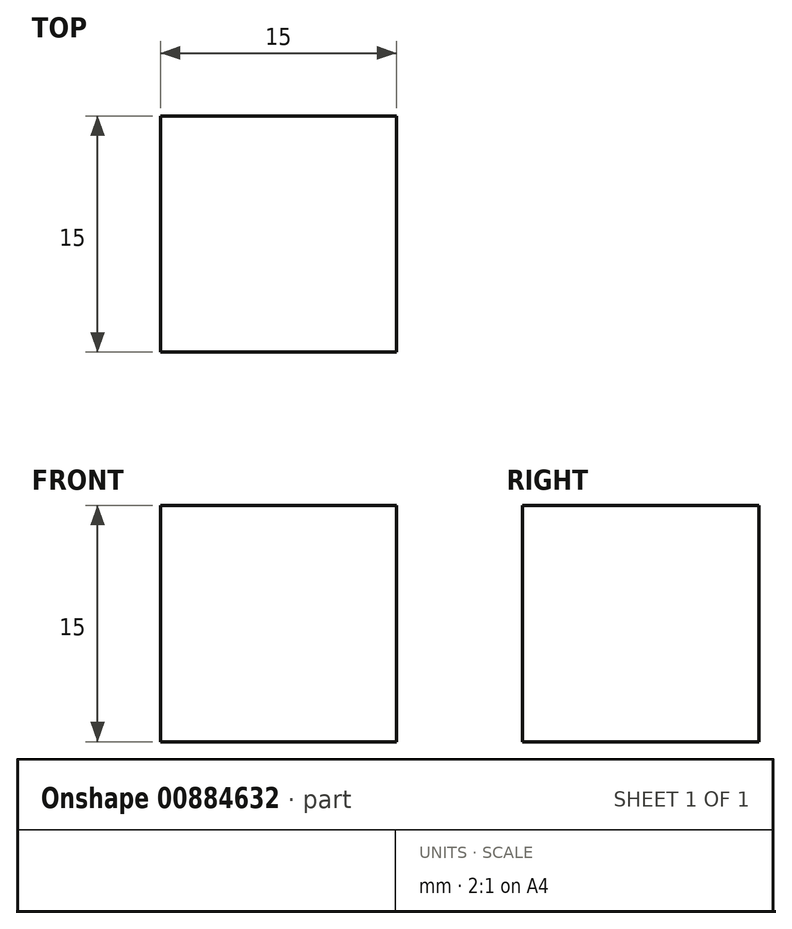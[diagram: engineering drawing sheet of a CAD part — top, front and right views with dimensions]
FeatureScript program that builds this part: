
annotation { "Feature Type Name" : "Feature", "Feature Type Description" : "" }
export const myFeature = defineFeature(function(context is Context, id is Id, definition is map)
    precondition{}
    {
        {
            var Q0;
            Q0=qCreatedBy(makeId("Front.planeOp"),FACE);
            var sketch = newSketch(context, id + "F0", { "sketchPlane" : qUnion([Q0])});
            skLineSegment(sketch, "E0.bottom", {"start": v(0, 0) * mm, "end": v(15, 0) * mm});
            skLineSegment(sketch, "E0.top", {"start": v(0, 15) * mm, "end": v(15, 15) * mm});
            skLineSegment(sketch, "E0.left", {"start": v(0, 0) * mm, "end": v(0, 15) * mm});
            skLineSegment(sketch, "E0.right", {"start": v(15, 0) * mm, "end": v(15, 15) * mm});
            skLineSegment(sketch, "E1.0.1.0", {"start": v(15, 15) * mm, "end": v(15, 30) * mm});
            skLineSegment(sketch, "E1.0.1.1", {"start": v(0, 15) * mm, "end": v(0, 30) * mm});
            skLineSegment(sketch, "E1.0.1.2", {"start": v(0, 30) * mm, "end": v(15, 30) * mm});
            skLineSegment(sketch, "E1.0.2.0", {"start": v(15, 30) * mm, "end": v(15, 45) * mm});
            skLineSegment(sketch, "E1.0.2.1", {"start": v(0, 30) * mm, "end": v(0, 45) * mm});
            skLineSegment(sketch, "E1.0.2.2", {"start": v(0, 45) * mm, "end": v(15, 45) * mm});
            skLineSegment(sketch, "E1.0.2.3", {"start": v(0, 30) * mm, "end": v(15, 30) * mm});
            skLineSegment(sketch, "E1.0.3.0", {"start": v(15, 45) * mm, "end": v(15, 60) * mm});
            skLineSegment(sketch, "E1.0.3.1", {"start": v(0, 45) * mm, "end": v(0, 60) * mm});
            skLineSegment(sketch, "E1.0.3.2", {"start": v(0, 60) * mm, "end": v(15, 60) * mm});
            skLineSegment(sketch, "E1.0.3.3", {"start": v(0, 45) * mm, "end": v(15, 45) * mm});
            skLineSegment(sketch, "E1.0.4.0", {"start": v(15, 60) * mm, "end": v(15, 75) * mm});
            skLineSegment(sketch, "E1.0.4.1", {"start": v(0, 60) * mm, "end": v(0, 75) * mm});
            skLineSegment(sketch, "E1.0.4.2", {"start": v(0, 75) * mm, "end": v(15, 75) * mm});
            skLineSegment(sketch, "E1.0.4.3", {"start": v(0, 60) * mm, "end": v(15, 60) * mm});
            skLineSegment(sketch, "E1.0.5.0", {"start": v(15, 75) * mm, "end": v(15, 90) * mm});
            skLineSegment(sketch, "E1.0.5.1", {"start": v(0, 75) * mm, "end": v(0, 90) * mm});
            skLineSegment(sketch, "E1.0.5.2", {"start": v(0, 90) * mm, "end": v(15, 90) * mm});
            skLineSegment(sketch, "E1.0.5.3", {"start": v(0, 75) * mm, "end": v(15, 75) * mm});
            skLineSegment(sketch, "E1.0.6.0", {"start": v(15, 90) * mm, "end": v(15, 105) * mm});
            skLineSegment(sketch, "E1.0.6.1", {"start": v(0, 90) * mm, "end": v(0, 105) * mm});
            skLineSegment(sketch, "E1.0.6.2", {"start": v(0, 105) * mm, "end": v(15, 105) * mm});
            skLineSegment(sketch, "E1.0.6.3", {"start": v(0, 90) * mm, "end": v(15, 90) * mm});
            skLineSegment(sketch, "E1.0.7.0", {"start": v(15, 105) * mm, "end": v(15, 120) * mm});
            skLineSegment(sketch, "E1.0.7.1", {"start": v(0, 105) * mm, "end": v(0, 120) * mm});
            skLineSegment(sketch, "E1.0.7.2", {"start": v(0, 120) * mm, "end": v(15, 120) * mm});
            skLineSegment(sketch, "E1.0.7.3", {"start": v(0, 105) * mm, "end": v(15, 105) * mm});
            skLineSegment(sketch, "E1.0.8.0", {"start": v(15, 120) * mm, "end": v(15, 135) * mm});
            skLineSegment(sketch, "E1.0.8.1", {"start": v(0, 120) * mm, "end": v(0, 135) * mm});
            skLineSegment(sketch, "E1.0.8.2", {"start": v(0, 135) * mm, "end": v(15, 135) * mm});
            skLineSegment(sketch, "E1.0.8.3", {"start": v(0, 120) * mm, "end": v(15, 120) * mm});
            skLineSegment(sketch, "E1.0.9.0", {"start": v(15, 135) * mm, "end": v(15, 150) * mm});
            skLineSegment(sketch, "E1.0.9.1", {"start": v(0, 135) * mm, "end": v(0, 150) * mm});
            skLineSegment(sketch, "E1.0.9.2", {"start": v(0, 150) * mm, "end": v(15, 150) * mm});
            skLineSegment(sketch, "E1.0.9.3", {"start": v(0, 135) * mm, "end": v(15, 135) * mm});
            skLineSegment(sketch, "E1.0.10.0", {"start": v(15, 150) * mm, "end": v(15, 165) * mm});
            skLineSegment(sketch, "E1.0.10.1", {"start": v(0, 150) * mm, "end": v(0, 165) * mm});
            skLineSegment(sketch, "E1.0.10.2", {"start": v(0, 165) * mm, "end": v(15, 165) * mm});
            skLineSegment(sketch, "E1.0.10.3", {"start": v(0, 150) * mm, "end": v(15, 150) * mm});
            skLineSegment(sketch, "E1.0.11.0", {"start": v(15, 165) * mm, "end": v(15, 180) * mm});
            skLineSegment(sketch, "E1.0.11.1", {"start": v(0, 165) * mm, "end": v(0, 180) * mm});
            skLineSegment(sketch, "E1.0.11.2", {"start": v(0, 180) * mm, "end": v(15, 180) * mm});
            skLineSegment(sketch, "E1.0.11.3", {"start": v(0, 165) * mm, "end": v(15, 165) * mm});
            skLineSegment(sketch, "E1.0.12.0", {"start": v(15, 180) * mm, "end": v(15, 195) * mm});
            skLineSegment(sketch, "E1.0.12.1", {"start": v(0, 180) * mm, "end": v(0, 195) * mm});
            skLineSegment(sketch, "E1.0.12.2", {"start": v(0, 195) * mm, "end": v(15, 195) * mm});
            skLineSegment(sketch, "E1.0.12.3", {"start": v(0, 180) * mm, "end": v(15, 180) * mm});
            skLineSegment(sketch, "E1.0.13.0", {"start": v(15, 195) * mm, "end": v(15, 210) * mm});
            skLineSegment(sketch, "E1.0.13.1", {"start": v(0, 195) * mm, "end": v(0, 210) * mm});
            skLineSegment(sketch, "E1.0.13.2", {"start": v(0, 210) * mm, "end": v(15, 210) * mm});
            skLineSegment(sketch, "E1.0.13.3", {"start": v(0, 195) * mm, "end": v(15, 195) * mm});
            skLineSegment(sketch, "E1.0.14.0", {"start": v(15, 210) * mm, "end": v(15, 225) * mm});
            skLineSegment(sketch, "E1.0.14.1", {"start": v(0, 210) * mm, "end": v(0, 225) * mm});
            skLineSegment(sketch, "E1.0.14.2", {"start": v(0, 225) * mm, "end": v(15, 225) * mm});
            skLineSegment(sketch, "E1.0.14.3", {"start": v(0, 210) * mm, "end": v(15, 210) * mm});
            skLineSegment(sketch, "E1.0.15.0", {"start": v(15, 225) * mm, "end": v(15, 240) * mm});
            skLineSegment(sketch, "E1.0.15.1", {"start": v(0, 225) * mm, "end": v(0, 240) * mm});
            skLineSegment(sketch, "E1.0.15.2", {"start": v(0, 240) * mm, "end": v(15, 240) * mm});
            skLineSegment(sketch, "E1.0.15.3", {"start": v(0, 225) * mm, "end": v(15, 225) * mm});
            skLineSegment(sketch, "E1.1.0.0", {"start": v(30, 0) * mm, "end": v(30, 15) * mm});
            skLineSegment(sketch, "E1.1.0.2", {"start": v(15, 15) * mm, "end": v(30, 15) * mm});
            skLineSegment(sketch, "E1.1.0.3", {"start": v(15, 0) * mm, "end": v(30, 0) * mm});
            skLineSegment(sketch, "E1.1.1.0", {"start": v(30, 15) * mm, "end": v(30, 30) * mm});
            skLineSegment(sketch, "E1.1.1.1", {"start": v(15, 15) * mm, "end": v(15, 30) * mm});
            skLineSegment(sketch, "E1.1.1.2", {"start": v(15, 30) * mm, "end": v(30, 30) * mm});
            skLineSegment(sketch, "E1.1.1.3", {"start": v(15, 15) * mm, "end": v(30, 15) * mm});
            skLineSegment(sketch, "E1.1.2.0", {"start": v(30, 30) * mm, "end": v(30, 45) * mm});
            skLineSegment(sketch, "E1.1.2.1", {"start": v(15, 30) * mm, "end": v(15, 45) * mm});
            skLineSegment(sketch, "E1.1.2.2", {"start": v(15, 45) * mm, "end": v(30, 45) * mm});
            skLineSegment(sketch, "E1.1.2.3", {"start": v(15, 30) * mm, "end": v(30, 30) * mm});
            skLineSegment(sketch, "E1.1.3.0", {"start": v(30, 45) * mm, "end": v(30, 60) * mm});
            skLineSegment(sketch, "E1.1.3.1", {"start": v(15, 45) * mm, "end": v(15, 60) * mm});
            skLineSegment(sketch, "E1.1.3.2", {"start": v(15, 60) * mm, "end": v(30, 60) * mm});
            skLineSegment(sketch, "E1.1.3.3", {"start": v(15, 45) * mm, "end": v(30, 45) * mm});
            skLineSegment(sketch, "E1.1.4.0", {"start": v(30, 60) * mm, "end": v(30, 75) * mm});
            skLineSegment(sketch, "E1.1.4.1", {"start": v(15, 60) * mm, "end": v(15, 75) * mm});
            skLineSegment(sketch, "E1.1.4.2", {"start": v(15, 75) * mm, "end": v(30, 75) * mm});
            skLineSegment(sketch, "E1.1.4.3", {"start": v(15, 60) * mm, "end": v(30, 60) * mm});
            skLineSegment(sketch, "E1.1.5.0", {"start": v(30, 75) * mm, "end": v(30, 90) * mm});
            skLineSegment(sketch, "E1.1.5.1", {"start": v(15, 75) * mm, "end": v(15, 90) * mm});
            skLineSegment(sketch, "E1.1.5.2", {"start": v(15, 90) * mm, "end": v(30, 90) * mm});
            skLineSegment(sketch, "E1.1.5.3", {"start": v(15, 75) * mm, "end": v(30, 75) * mm});
            skLineSegment(sketch, "E1.1.6.0", {"start": v(30, 90) * mm, "end": v(30, 105) * mm});
            skLineSegment(sketch, "E1.1.6.1", {"start": v(15, 90) * mm, "end": v(15, 105) * mm});
            skLineSegment(sketch, "E1.1.6.2", {"start": v(15, 105) * mm, "end": v(30, 105) * mm});
            skLineSegment(sketch, "E1.1.6.3", {"start": v(15, 90) * mm, "end": v(30, 90) * mm});
            skLineSegment(sketch, "E1.1.7.0", {"start": v(30, 105) * mm, "end": v(30, 120) * mm});
            skLineSegment(sketch, "E1.1.7.1", {"start": v(15, 105) * mm, "end": v(15, 120) * mm});
            skLineSegment(sketch, "E1.1.7.2", {"start": v(15, 120) * mm, "end": v(30, 120) * mm});
            skLineSegment(sketch, "E1.1.7.3", {"start": v(15, 105) * mm, "end": v(30, 105) * mm});
            skLineSegment(sketch, "E1.1.8.0", {"start": v(30, 120) * mm, "end": v(30, 135) * mm});
            skLineSegment(sketch, "E1.1.8.1", {"start": v(15, 120) * mm, "end": v(15, 135) * mm});
            skLineSegment(sketch, "E1.1.8.2", {"start": v(15, 135) * mm, "end": v(30, 135) * mm});
            skLineSegment(sketch, "E1.1.8.3", {"start": v(15, 120) * mm, "end": v(30, 120) * mm});
            skLineSegment(sketch, "E1.1.9.0", {"start": v(30, 135) * mm, "end": v(30, 150) * mm});
            skLineSegment(sketch, "E1.1.9.1", {"start": v(15, 135) * mm, "end": v(15, 150) * mm});
            skLineSegment(sketch, "E1.1.9.2", {"start": v(15, 150) * mm, "end": v(30, 150) * mm});
            skLineSegment(sketch, "E1.1.9.3", {"start": v(15, 135) * mm, "end": v(30, 135) * mm});
            skLineSegment(sketch, "E1.1.10.0", {"start": v(30, 150) * mm, "end": v(30, 165) * mm});
            skLineSegment(sketch, "E1.1.10.1", {"start": v(15, 150) * mm, "end": v(15, 165) * mm});
            skLineSegment(sketch, "E1.1.10.2", {"start": v(15, 165) * mm, "end": v(30, 165) * mm});
            skLineSegment(sketch, "E1.1.10.3", {"start": v(15, 150) * mm, "end": v(30, 150) * mm});
            skLineSegment(sketch, "E1.1.11.0", {"start": v(30, 165) * mm, "end": v(30, 180) * mm});
            skLineSegment(sketch, "E1.1.11.1", {"start": v(15, 165) * mm, "end": v(15, 180) * mm});
            skLineSegment(sketch, "E1.1.11.2", {"start": v(15, 180) * mm, "end": v(30, 180) * mm});
            skLineSegment(sketch, "E1.1.11.3", {"start": v(15, 165) * mm, "end": v(30, 165) * mm});
            skLineSegment(sketch, "E1.1.12.0", {"start": v(30, 180) * mm, "end": v(30, 195) * mm});
            skLineSegment(sketch, "E1.1.12.1", {"start": v(15, 180) * mm, "end": v(15, 195) * mm});
            skLineSegment(sketch, "E1.1.12.2", {"start": v(15, 195) * mm, "end": v(30, 195) * mm});
            skLineSegment(sketch, "E1.1.12.3", {"start": v(15, 180) * mm, "end": v(30, 180) * mm});
            skLineSegment(sketch, "E1.1.13.0", {"start": v(30, 195) * mm, "end": v(30, 210) * mm});
            skLineSegment(sketch, "E1.1.13.1", {"start": v(15, 195) * mm, "end": v(15, 210) * mm});
            skLineSegment(sketch, "E1.1.13.2", {"start": v(15, 210) * mm, "end": v(30, 210) * mm});
            skLineSegment(sketch, "E1.1.13.3", {"start": v(15, 195) * mm, "end": v(30, 195) * mm});
            skLineSegment(sketch, "E1.1.14.0", {"start": v(30, 210) * mm, "end": v(30, 225) * mm});
            skLineSegment(sketch, "E1.1.14.1", {"start": v(15, 210) * mm, "end": v(15, 225) * mm});
            skLineSegment(sketch, "E1.1.14.2", {"start": v(15, 225) * mm, "end": v(30, 225) * mm});
            skLineSegment(sketch, "E1.1.14.3", {"start": v(15, 210) * mm, "end": v(30, 210) * mm});
            skLineSegment(sketch, "E1.1.15.0", {"start": v(30, 225) * mm, "end": v(30, 240) * mm});
            skLineSegment(sketch, "E1.1.15.1", {"start": v(15, 225) * mm, "end": v(15, 240) * mm});
            skLineSegment(sketch, "E1.1.15.2", {"start": v(15, 240) * mm, "end": v(30, 240) * mm});
            skLineSegment(sketch, "E1.1.15.3", {"start": v(15, 225) * mm, "end": v(30, 225) * mm});
            skLineSegment(sketch, "E1.2.0.0", {"start": v(45, 0) * mm, "end": v(45, 15) * mm});
            skLineSegment(sketch, "E1.2.0.1", {"start": v(30, 0) * mm, "end": v(30, 15) * mm});
            skLineSegment(sketch, "E1.2.0.2", {"start": v(30, 15) * mm, "end": v(45, 15) * mm});
            skLineSegment(sketch, "E1.2.0.3", {"start": v(30, 0) * mm, "end": v(45, 0) * mm});
            skLineSegment(sketch, "E1.2.1.0", {"start": v(45, 15) * mm, "end": v(45, 30) * mm});
            skLineSegment(sketch, "E1.2.1.1", {"start": v(30, 15) * mm, "end": v(30, 30) * mm});
            skLineSegment(sketch, "E1.2.1.2", {"start": v(30, 30) * mm, "end": v(45, 30) * mm});
            skLineSegment(sketch, "E1.2.1.3", {"start": v(30, 15) * mm, "end": v(45, 15) * mm});
            skLineSegment(sketch, "E1.2.2.0", {"start": v(45, 30) * mm, "end": v(45, 45) * mm});
            skLineSegment(sketch, "E1.2.2.1", {"start": v(30, 30) * mm, "end": v(30, 45) * mm});
            skLineSegment(sketch, "E1.2.2.2", {"start": v(30, 45) * mm, "end": v(45, 45) * mm});
            skLineSegment(sketch, "E1.2.2.3", {"start": v(30, 30) * mm, "end": v(45, 30) * mm});
            skLineSegment(sketch, "E1.2.3.0", {"start": v(45, 45) * mm, "end": v(45, 60) * mm});
            skLineSegment(sketch, "E1.2.3.1", {"start": v(30, 45) * mm, "end": v(30, 60) * mm});
            skLineSegment(sketch, "E1.2.3.2", {"start": v(30, 60) * mm, "end": v(45, 60) * mm});
            skLineSegment(sketch, "E1.2.3.3", {"start": v(30, 45) * mm, "end": v(45, 45) * mm});
            skLineSegment(sketch, "E1.2.4.0", {"start": v(45, 60) * mm, "end": v(45, 75) * mm});
            skLineSegment(sketch, "E1.2.4.1", {"start": v(30, 60) * mm, "end": v(30, 75) * mm});
            skLineSegment(sketch, "E1.2.4.2", {"start": v(30, 75) * mm, "end": v(45, 75) * mm});
            skLineSegment(sketch, "E1.2.4.3", {"start": v(30, 60) * mm, "end": v(45, 60) * mm});
            skLineSegment(sketch, "E1.2.5.0", {"start": v(45, 75) * mm, "end": v(45, 90) * mm});
            skLineSegment(sketch, "E1.2.5.1", {"start": v(30, 75) * mm, "end": v(30, 90) * mm});
            skLineSegment(sketch, "E1.2.5.2", {"start": v(30, 90) * mm, "end": v(45, 90) * mm});
            skLineSegment(sketch, "E1.2.5.3", {"start": v(30, 75) * mm, "end": v(45, 75) * mm});
            skLineSegment(sketch, "E1.2.6.0", {"start": v(45, 90) * mm, "end": v(45, 105) * mm});
            skLineSegment(sketch, "E1.2.6.1", {"start": v(30, 90) * mm, "end": v(30, 105) * mm});
            skLineSegment(sketch, "E1.2.6.2", {"start": v(30, 105) * mm, "end": v(45, 105) * mm});
            skLineSegment(sketch, "E1.2.6.3", {"start": v(30, 90) * mm, "end": v(45, 90) * mm});
            skLineSegment(sketch, "E1.2.7.0", {"start": v(45, 105) * mm, "end": v(45, 120) * mm});
            skLineSegment(sketch, "E1.2.7.1", {"start": v(30, 105) * mm, "end": v(30, 120) * mm});
            skLineSegment(sketch, "E1.2.7.2", {"start": v(30, 120) * mm, "end": v(45, 120) * mm});
            skLineSegment(sketch, "E1.2.7.3", {"start": v(30, 105) * mm, "end": v(45, 105) * mm});
            skLineSegment(sketch, "E1.2.8.0", {"start": v(45, 120) * mm, "end": v(45, 135) * mm});
            skLineSegment(sketch, "E1.2.8.1", {"start": v(30, 120) * mm, "end": v(30, 135) * mm});
            skLineSegment(sketch, "E1.2.8.2", {"start": v(30, 135) * mm, "end": v(45, 135) * mm});
            skLineSegment(sketch, "E1.2.8.3", {"start": v(30, 120) * mm, "end": v(45, 120) * mm});
            skLineSegment(sketch, "E1.2.9.0", {"start": v(45, 135) * mm, "end": v(45, 150) * mm});
            skLineSegment(sketch, "E1.2.9.1", {"start": v(30, 135) * mm, "end": v(30, 150) * mm});
            skLineSegment(sketch, "E1.2.9.2", {"start": v(30, 150) * mm, "end": v(45, 150) * mm});
            skLineSegment(sketch, "E1.2.9.3", {"start": v(30, 135) * mm, "end": v(45, 135) * mm});
            skLineSegment(sketch, "E1.2.10.0", {"start": v(45, 150) * mm, "end": v(45, 165) * mm});
            skLineSegment(sketch, "E1.2.10.1", {"start": v(30, 150) * mm, "end": v(30, 165) * mm});
            skLineSegment(sketch, "E1.2.10.2", {"start": v(30, 165) * mm, "end": v(45, 165) * mm});
            skLineSegment(sketch, "E1.2.10.3", {"start": v(30, 150) * mm, "end": v(45, 150) * mm});
            skLineSegment(sketch, "E1.2.11.0", {"start": v(45, 165) * mm, "end": v(45, 180) * mm});
            skLineSegment(sketch, "E1.2.11.1", {"start": v(30, 165) * mm, "end": v(30, 180) * mm});
            skLineSegment(sketch, "E1.2.11.2", {"start": v(30, 180) * mm, "end": v(45, 180) * mm});
            skLineSegment(sketch, "E1.2.11.3", {"start": v(30, 165) * mm, "end": v(45, 165) * mm});
            skLineSegment(sketch, "E1.2.12.0", {"start": v(45, 180) * mm, "end": v(45, 195) * mm});
            skLineSegment(sketch, "E1.2.12.1", {"start": v(30, 180) * mm, "end": v(30, 195) * mm});
            skLineSegment(sketch, "E1.2.12.2", {"start": v(30, 195) * mm, "end": v(45, 195) * mm});
            skLineSegment(sketch, "E1.2.12.3", {"start": v(30, 180) * mm, "end": v(45, 180) * mm});
            skLineSegment(sketch, "E1.2.13.0", {"start": v(45, 195) * mm, "end": v(45, 210) * mm});
            skLineSegment(sketch, "E1.2.13.1", {"start": v(30, 195) * mm, "end": v(30, 210) * mm});
            skLineSegment(sketch, "E1.2.13.2", {"start": v(30, 210) * mm, "end": v(45, 210) * mm});
            skLineSegment(sketch, "E1.2.13.3", {"start": v(30, 195) * mm, "end": v(45, 195) * mm});
            skLineSegment(sketch, "E1.2.14.0", {"start": v(45, 210) * mm, "end": v(45, 225) * mm});
            skLineSegment(sketch, "E1.2.14.1", {"start": v(30, 210) * mm, "end": v(30, 225) * mm});
            skLineSegment(sketch, "E1.2.14.2", {"start": v(30, 225) * mm, "end": v(45, 225) * mm});
            skLineSegment(sketch, "E1.2.14.3", {"start": v(30, 210) * mm, "end": v(45, 210) * mm});
            skLineSegment(sketch, "E1.2.15.0", {"start": v(45, 225) * mm, "end": v(45, 240) * mm});
            skLineSegment(sketch, "E1.2.15.1", {"start": v(30, 225) * mm, "end": v(30, 240) * mm});
            skLineSegment(sketch, "E1.2.15.2", {"start": v(30, 240) * mm, "end": v(45, 240) * mm});
            skLineSegment(sketch, "E1.2.15.3", {"start": v(30, 225) * mm, "end": v(45, 225) * mm});
            skLineSegment(sketch, "E1.3.0.0", {"start": v(60, 0) * mm, "end": v(60, 15) * mm});
            skLineSegment(sketch, "E1.3.0.1", {"start": v(45, 0) * mm, "end": v(45, 15) * mm});
            skLineSegment(sketch, "E1.3.0.2", {"start": v(45, 15) * mm, "end": v(60, 15) * mm});
            skLineSegment(sketch, "E1.3.0.3", {"start": v(45, 0) * mm, "end": v(60, 0) * mm});
            skLineSegment(sketch, "E1.3.1.0", {"start": v(60, 15) * mm, "end": v(60, 30) * mm});
            skLineSegment(sketch, "E1.3.1.1", {"start": v(45, 15) * mm, "end": v(45, 30) * mm});
            skLineSegment(sketch, "E1.3.1.2", {"start": v(45, 30) * mm, "end": v(60, 30) * mm});
            skLineSegment(sketch, "E1.3.1.3", {"start": v(45, 15) * mm, "end": v(60, 15) * mm});
            skLineSegment(sketch, "E1.3.2.0", {"start": v(60, 30) * mm, "end": v(60, 45) * mm});
            skLineSegment(sketch, "E1.3.2.1", {"start": v(45, 30) * mm, "end": v(45, 45) * mm});
            skLineSegment(sketch, "E1.3.2.2", {"start": v(45, 45) * mm, "end": v(60, 45) * mm});
            skLineSegment(sketch, "E1.3.2.3", {"start": v(45, 30) * mm, "end": v(60, 30) * mm});
            skLineSegment(sketch, "E1.3.3.0", {"start": v(60, 45) * mm, "end": v(60, 60) * mm});
            skLineSegment(sketch, "E1.3.3.1", {"start": v(45, 45) * mm, "end": v(45, 60) * mm});
            skLineSegment(sketch, "E1.3.3.2", {"start": v(45, 60) * mm, "end": v(60, 60) * mm});
            skLineSegment(sketch, "E1.3.3.3", {"start": v(45, 45) * mm, "end": v(60, 45) * mm});
            skLineSegment(sketch, "E1.3.4.0", {"start": v(60, 60) * mm, "end": v(60, 75) * mm});
            skLineSegment(sketch, "E1.3.4.1", {"start": v(45, 60) * mm, "end": v(45, 75) * mm});
            skLineSegment(sketch, "E1.3.4.2", {"start": v(45, 75) * mm, "end": v(60, 75) * mm});
            skLineSegment(sketch, "E1.3.4.3", {"start": v(45, 60) * mm, "end": v(60, 60) * mm});
            skLineSegment(sketch, "E1.3.5.0", {"start": v(60, 75) * mm, "end": v(60, 90) * mm});
            skLineSegment(sketch, "E1.3.5.1", {"start": v(45, 75) * mm, "end": v(45, 90) * mm});
            skLineSegment(sketch, "E1.3.5.2", {"start": v(45, 90) * mm, "end": v(60, 90) * mm});
            skLineSegment(sketch, "E1.3.5.3", {"start": v(45, 75) * mm, "end": v(60, 75) * mm});
            skLineSegment(sketch, "E1.3.6.0", {"start": v(60, 90) * mm, "end": v(60, 105) * mm});
            skLineSegment(sketch, "E1.3.6.1", {"start": v(45, 90) * mm, "end": v(45, 105) * mm});
            skLineSegment(sketch, "E1.3.6.2", {"start": v(45, 105) * mm, "end": v(60, 105) * mm});
            skLineSegment(sketch, "E1.3.6.3", {"start": v(45, 90) * mm, "end": v(60, 90) * mm});
            skLineSegment(sketch, "E1.3.7.0", {"start": v(60, 105) * mm, "end": v(60, 120) * mm});
            skLineSegment(sketch, "E1.3.7.1", {"start": v(45, 105) * mm, "end": v(45, 120) * mm});
            skLineSegment(sketch, "E1.3.7.2", {"start": v(45, 120) * mm, "end": v(60, 120) * mm});
            skLineSegment(sketch, "E1.3.7.3", {"start": v(45, 105) * mm, "end": v(60, 105) * mm});
            skLineSegment(sketch, "E1.3.8.0", {"start": v(60, 120) * mm, "end": v(60, 135) * mm});
            skLineSegment(sketch, "E1.3.8.1", {"start": v(45, 120) * mm, "end": v(45, 135) * mm});
            skLineSegment(sketch, "E1.3.8.2", {"start": v(45, 135) * mm, "end": v(60, 135) * mm});
            skLineSegment(sketch, "E1.3.8.3", {"start": v(45, 120) * mm, "end": v(60, 120) * mm});
            skLineSegment(sketch, "E1.3.9.0", {"start": v(60, 135) * mm, "end": v(60, 150) * mm});
            skLineSegment(sketch, "E1.3.9.1", {"start": v(45, 135) * mm, "end": v(45, 150) * mm});
            skLineSegment(sketch, "E1.3.9.2", {"start": v(45, 150) * mm, "end": v(60, 150) * mm});
            skLineSegment(sketch, "E1.3.9.3", {"start": v(45, 135) * mm, "end": v(60, 135) * mm});
            skLineSegment(sketch, "E1.3.10.0", {"start": v(60, 150) * mm, "end": v(60, 165) * mm});
            skLineSegment(sketch, "E1.3.10.1", {"start": v(45, 150) * mm, "end": v(45, 165) * mm});
            skLineSegment(sketch, "E1.3.10.2", {"start": v(45, 165) * mm, "end": v(60, 165) * mm});
            skLineSegment(sketch, "E1.3.10.3", {"start": v(45, 150) * mm, "end": v(60, 150) * mm});
            skLineSegment(sketch, "E1.3.11.0", {"start": v(60, 165) * mm, "end": v(60, 180) * mm});
            skLineSegment(sketch, "E1.3.11.1", {"start": v(45, 165) * mm, "end": v(45, 180) * mm});
            skLineSegment(sketch, "E1.3.11.2", {"start": v(45, 180) * mm, "end": v(60, 180) * mm});
            skLineSegment(sketch, "E1.3.11.3", {"start": v(45, 165) * mm, "end": v(60, 165) * mm});
            skLineSegment(sketch, "E1.3.12.0", {"start": v(60, 180) * mm, "end": v(60, 195) * mm});
            skLineSegment(sketch, "E1.3.12.1", {"start": v(45, 180) * mm, "end": v(45, 195) * mm});
            skLineSegment(sketch, "E1.3.12.2", {"start": v(45, 195) * mm, "end": v(60, 195) * mm});
            skLineSegment(sketch, "E1.3.12.3", {"start": v(45, 180) * mm, "end": v(60, 180) * mm});
            skLineSegment(sketch, "E1.3.13.0", {"start": v(60, 195) * mm, "end": v(60, 210) * mm});
            skLineSegment(sketch, "E1.3.13.1", {"start": v(45, 195) * mm, "end": v(45, 210) * mm});
            skLineSegment(sketch, "E1.3.13.2", {"start": v(45, 210) * mm, "end": v(60, 210) * mm});
            skLineSegment(sketch, "E1.3.13.3", {"start": v(45, 195) * mm, "end": v(60, 195) * mm});
            skLineSegment(sketch, "E1.3.14.0", {"start": v(60, 210) * mm, "end": v(60, 225) * mm});
            skLineSegment(sketch, "E1.3.14.1", {"start": v(45, 210) * mm, "end": v(45, 225) * mm});
            skLineSegment(sketch, "E1.3.14.2", {"start": v(45, 225) * mm, "end": v(60, 225) * mm});
            skLineSegment(sketch, "E1.3.14.3", {"start": v(45, 210) * mm, "end": v(60, 210) * mm});
            skLineSegment(sketch, "E1.3.15.0", {"start": v(60, 225) * mm, "end": v(60, 240) * mm});
            skLineSegment(sketch, "E1.3.15.1", {"start": v(45, 225) * mm, "end": v(45, 240) * mm});
            skLineSegment(sketch, "E1.3.15.2", {"start": v(45, 240) * mm, "end": v(60, 240) * mm});
            skLineSegment(sketch, "E1.3.15.3", {"start": v(45, 225) * mm, "end": v(60, 225) * mm});
            skLineSegment(sketch, "E1.4.0.0", {"start": v(75, 0) * mm, "end": v(75, 15) * mm});
            skLineSegment(sketch, "E1.4.0.1", {"start": v(60, 0) * mm, "end": v(60, 15) * mm});
            skLineSegment(sketch, "E1.4.0.2", {"start": v(60, 15) * mm, "end": v(75, 15) * mm});
            skLineSegment(sketch, "E1.4.0.3", {"start": v(60, 0) * mm, "end": v(75, 0) * mm});
            skLineSegment(sketch, "E1.4.1.0", {"start": v(75, 15) * mm, "end": v(75, 30) * mm});
            skLineSegment(sketch, "E1.4.1.1", {"start": v(60, 15) * mm, "end": v(60, 30) * mm});
            skLineSegment(sketch, "E1.4.1.2", {"start": v(60, 30) * mm, "end": v(75, 30) * mm});
            skLineSegment(sketch, "E1.4.1.3", {"start": v(60, 15) * mm, "end": v(75, 15) * mm});
            skLineSegment(sketch, "E1.4.2.0", {"start": v(75, 30) * mm, "end": v(75, 45) * mm});
            skLineSegment(sketch, "E1.4.2.1", {"start": v(60, 30) * mm, "end": v(60, 45) * mm});
            skLineSegment(sketch, "E1.4.2.2", {"start": v(60, 45) * mm, "end": v(75, 45) * mm});
            skLineSegment(sketch, "E1.4.2.3", {"start": v(60, 30) * mm, "end": v(75, 30) * mm});
            skLineSegment(sketch, "E1.4.3.0", {"start": v(75, 45) * mm, "end": v(75, 60) * mm});
            skLineSegment(sketch, "E1.4.3.1", {"start": v(60, 45) * mm, "end": v(60, 60) * mm});
            skLineSegment(sketch, "E1.4.3.2", {"start": v(60, 60) * mm, "end": v(75, 60) * mm});
            skLineSegment(sketch, "E1.4.3.3", {"start": v(60, 45) * mm, "end": v(75, 45) * mm});
            skLineSegment(sketch, "E1.4.4.0", {"start": v(75, 60) * mm, "end": v(75, 75) * mm});
            skLineSegment(sketch, "E1.4.4.1", {"start": v(60, 60) * mm, "end": v(60, 75) * mm});
            skLineSegment(sketch, "E1.4.4.2", {"start": v(60, 75) * mm, "end": v(75, 75) * mm});
            skLineSegment(sketch, "E1.4.4.3", {"start": v(60, 60) * mm, "end": v(75, 60) * mm});
            skLineSegment(sketch, "E1.4.5.0", {"start": v(75, 75) * mm, "end": v(75, 90) * mm});
            skLineSegment(sketch, "E1.4.5.1", {"start": v(60, 75) * mm, "end": v(60, 90) * mm});
            skLineSegment(sketch, "E1.4.5.2", {"start": v(60, 90) * mm, "end": v(75, 90) * mm});
            skLineSegment(sketch, "E1.4.5.3", {"start": v(60, 75) * mm, "end": v(75, 75) * mm});
            skLineSegment(sketch, "E1.4.6.0", {"start": v(75, 90) * mm, "end": v(75, 105) * mm});
            skLineSegment(sketch, "E1.4.6.1", {"start": v(60, 90) * mm, "end": v(60, 105) * mm});
            skLineSegment(sketch, "E1.4.6.2", {"start": v(60, 105) * mm, "end": v(75, 105) * mm});
            skLineSegment(sketch, "E1.4.6.3", {"start": v(60, 90) * mm, "end": v(75, 90) * mm});
            skLineSegment(sketch, "E1.4.7.0", {"start": v(75, 105) * mm, "end": v(75, 120) * mm});
            skLineSegment(sketch, "E1.4.7.1", {"start": v(60, 105) * mm, "end": v(60, 120) * mm});
            skLineSegment(sketch, "E1.4.7.2", {"start": v(60, 120) * mm, "end": v(75, 120) * mm});
            skLineSegment(sketch, "E1.4.7.3", {"start": v(60, 105) * mm, "end": v(75, 105) * mm});
            skLineSegment(sketch, "E1.4.8.0", {"start": v(75, 120) * mm, "end": v(75, 135) * mm});
            skLineSegment(sketch, "E1.4.8.1", {"start": v(60, 120) * mm, "end": v(60, 135) * mm});
            skLineSegment(sketch, "E1.4.8.2", {"start": v(60, 135) * mm, "end": v(75, 135) * mm});
            skLineSegment(sketch, "E1.4.8.3", {"start": v(60, 120) * mm, "end": v(75, 120) * mm});
            skLineSegment(sketch, "E1.4.9.0", {"start": v(75, 135) * mm, "end": v(75, 150) * mm});
            skLineSegment(sketch, "E1.4.9.1", {"start": v(60, 135) * mm, "end": v(60, 150) * mm});
            skLineSegment(sketch, "E1.4.9.2", {"start": v(60, 150) * mm, "end": v(75, 150) * mm});
            skLineSegment(sketch, "E1.4.9.3", {"start": v(60, 135) * mm, "end": v(75, 135) * mm});
            skLineSegment(sketch, "E1.4.10.0", {"start": v(75, 150) * mm, "end": v(75, 165) * mm});
            skLineSegment(sketch, "E1.4.10.1", {"start": v(60, 150) * mm, "end": v(60, 165) * mm});
            skLineSegment(sketch, "E1.4.10.2", {"start": v(60, 165) * mm, "end": v(75, 165) * mm});
            skLineSegment(sketch, "E1.4.10.3", {"start": v(60, 150) * mm, "end": v(75, 150) * mm});
            skLineSegment(sketch, "E1.4.11.0", {"start": v(75, 165) * mm, "end": v(75, 180) * mm});
            skLineSegment(sketch, "E1.4.11.1", {"start": v(60, 165) * mm, "end": v(60, 180) * mm});
            skLineSegment(sketch, "E1.4.11.2", {"start": v(60, 180) * mm, "end": v(75, 180) * mm});
            skLineSegment(sketch, "E1.4.11.3", {"start": v(60, 165) * mm, "end": v(75, 165) * mm});
            skLineSegment(sketch, "E1.4.12.0", {"start": v(75, 180) * mm, "end": v(75, 195) * mm});
            skLineSegment(sketch, "E1.4.12.1", {"start": v(60, 180) * mm, "end": v(60, 195) * mm});
            skLineSegment(sketch, "E1.4.12.2", {"start": v(60, 195) * mm, "end": v(75, 195) * mm});
            skLineSegment(sketch, "E1.4.12.3", {"start": v(60, 180) * mm, "end": v(75, 180) * mm});
            skLineSegment(sketch, "E1.4.13.0", {"start": v(75, 195) * mm, "end": v(75, 210) * mm});
            skLineSegment(sketch, "E1.4.13.1", {"start": v(60, 195) * mm, "end": v(60, 210) * mm});
            skLineSegment(sketch, "E1.4.13.2", {"start": v(60, 210) * mm, "end": v(75, 210) * mm});
            skLineSegment(sketch, "E1.4.13.3", {"start": v(60, 195) * mm, "end": v(75, 195) * mm});
            skLineSegment(sketch, "E1.4.14.0", {"start": v(75, 210) * mm, "end": v(75, 225) * mm});
            skLineSegment(sketch, "E1.4.14.1", {"start": v(60, 210) * mm, "end": v(60, 225) * mm});
            skLineSegment(sketch, "E1.4.14.2", {"start": v(60, 225) * mm, "end": v(75, 225) * mm});
            skLineSegment(sketch, "E1.4.14.3", {"start": v(60, 210) * mm, "end": v(75, 210) * mm});
            skLineSegment(sketch, "E1.4.15.0", {"start": v(75, 225) * mm, "end": v(75, 240) * mm});
            skLineSegment(sketch, "E1.4.15.1", {"start": v(60, 225) * mm, "end": v(60, 240) * mm});
            skLineSegment(sketch, "E1.4.15.2", {"start": v(60, 240) * mm, "end": v(75, 240) * mm});
            skLineSegment(sketch, "E1.4.15.3", {"start": v(60, 225) * mm, "end": v(75, 225) * mm});
            skLineSegment(sketch, "E1.5.0.0", {"start": v(90, 0) * mm, "end": v(90, 15) * mm});
            skLineSegment(sketch, "E1.5.0.1", {"start": v(75, 0) * mm, "end": v(75, 15) * mm});
            skLineSegment(sketch, "E1.5.0.2", {"start": v(75, 15) * mm, "end": v(90, 15) * mm});
            skLineSegment(sketch, "E1.5.0.3", {"start": v(75, 0) * mm, "end": v(90, 0) * mm});
            skLineSegment(sketch, "E1.5.1.0", {"start": v(90, 15) * mm, "end": v(90, 30) * mm});
            skLineSegment(sketch, "E1.5.1.1", {"start": v(75, 15) * mm, "end": v(75, 30) * mm});
            skLineSegment(sketch, "E1.5.1.2", {"start": v(75, 30) * mm, "end": v(90, 30) * mm});
            skLineSegment(sketch, "E1.5.1.3", {"start": v(75, 15) * mm, "end": v(90, 15) * mm});
            skLineSegment(sketch, "E1.5.2.0", {"start": v(90, 30) * mm, "end": v(90, 45) * mm});
            skLineSegment(sketch, "E1.5.2.1", {"start": v(75, 30) * mm, "end": v(75, 45) * mm});
            skLineSegment(sketch, "E1.5.2.2", {"start": v(75, 45) * mm, "end": v(90, 45) * mm});
            skLineSegment(sketch, "E1.5.2.3", {"start": v(75, 30) * mm, "end": v(90, 30) * mm});
            skLineSegment(sketch, "E1.5.3.0", {"start": v(90, 45) * mm, "end": v(90, 60) * mm});
            skLineSegment(sketch, "E1.5.3.1", {"start": v(75, 45) * mm, "end": v(75, 60) * mm});
            skLineSegment(sketch, "E1.5.3.2", {"start": v(75, 60) * mm, "end": v(90, 60) * mm});
            skLineSegment(sketch, "E1.5.3.3", {"start": v(75, 45) * mm, "end": v(90, 45) * mm});
            skLineSegment(sketch, "E1.5.4.0", {"start": v(90, 60) * mm, "end": v(90, 75) * mm});
            skLineSegment(sketch, "E1.5.4.1", {"start": v(75, 60) * mm, "end": v(75, 75) * mm});
            skLineSegment(sketch, "E1.5.4.2", {"start": v(75, 75) * mm, "end": v(90, 75) * mm});
            skLineSegment(sketch, "E1.5.4.3", {"start": v(75, 60) * mm, "end": v(90, 60) * mm});
            skLineSegment(sketch, "E1.5.5.0", {"start": v(90, 75) * mm, "end": v(90, 90) * mm});
            skLineSegment(sketch, "E1.5.5.1", {"start": v(75, 75) * mm, "end": v(75, 90) * mm});
            skLineSegment(sketch, "E1.5.5.2", {"start": v(75, 90) * mm, "end": v(90, 90) * mm});
            skLineSegment(sketch, "E1.5.5.3", {"start": v(75, 75) * mm, "end": v(90, 75) * mm});
            skLineSegment(sketch, "E1.5.6.0", {"start": v(90, 90) * mm, "end": v(90, 105) * mm});
            skLineSegment(sketch, "E1.5.6.1", {"start": v(75, 90) * mm, "end": v(75, 105) * mm});
            skLineSegment(sketch, "E1.5.6.2", {"start": v(75, 105) * mm, "end": v(90, 105) * mm});
            skLineSegment(sketch, "E1.5.6.3", {"start": v(75, 90) * mm, "end": v(90, 90) * mm});
            skLineSegment(sketch, "E1.5.7.0", {"start": v(90, 105) * mm, "end": v(90, 120) * mm});
            skLineSegment(sketch, "E1.5.7.1", {"start": v(75, 105) * mm, "end": v(75, 120) * mm});
            skLineSegment(sketch, "E1.5.7.2", {"start": v(75, 120) * mm, "end": v(90, 120) * mm});
            skLineSegment(sketch, "E1.5.7.3", {"start": v(75, 105) * mm, "end": v(90, 105) * mm});
            skLineSegment(sketch, "E1.5.8.0", {"start": v(90, 120) * mm, "end": v(90, 135) * mm});
            skLineSegment(sketch, "E1.5.8.1", {"start": v(75, 120) * mm, "end": v(75, 135) * mm});
            skLineSegment(sketch, "E1.5.8.2", {"start": v(75, 135) * mm, "end": v(90, 135) * mm});
            skLineSegment(sketch, "E1.5.8.3", {"start": v(75, 120) * mm, "end": v(90, 120) * mm});
            skLineSegment(sketch, "E1.5.9.0", {"start": v(90, 135) * mm, "end": v(90, 150) * mm});
            skLineSegment(sketch, "E1.5.9.1", {"start": v(75, 135) * mm, "end": v(75, 150) * mm});
            skLineSegment(sketch, "E1.5.9.2", {"start": v(75, 150) * mm, "end": v(90, 150) * mm});
            skLineSegment(sketch, "E1.5.9.3", {"start": v(75, 135) * mm, "end": v(90, 135) * mm});
            skLineSegment(sketch, "E1.5.10.0", {"start": v(90, 150) * mm, "end": v(90, 165) * mm});
            skLineSegment(sketch, "E1.5.10.1", {"start": v(75, 150) * mm, "end": v(75, 165) * mm});
            skLineSegment(sketch, "E1.5.10.2", {"start": v(75, 165) * mm, "end": v(90, 165) * mm});
            skLineSegment(sketch, "E1.5.10.3", {"start": v(75, 150) * mm, "end": v(90, 150) * mm});
            skLineSegment(sketch, "E1.5.11.0", {"start": v(90, 165) * mm, "end": v(90, 180) * mm});
            skLineSegment(sketch, "E1.5.11.1", {"start": v(75, 165) * mm, "end": v(75, 180) * mm});
            skLineSegment(sketch, "E1.5.11.2", {"start": v(75, 180) * mm, "end": v(90, 180) * mm});
            skLineSegment(sketch, "E1.5.11.3", {"start": v(75, 165) * mm, "end": v(90, 165) * mm});
            skLineSegment(sketch, "E1.5.12.0", {"start": v(90, 180) * mm, "end": v(90, 195) * mm});
            skLineSegment(sketch, "E1.5.12.1", {"start": v(75, 180) * mm, "end": v(75, 195) * mm});
            skLineSegment(sketch, "E1.5.12.2", {"start": v(75, 195) * mm, "end": v(90, 195) * mm});
            skLineSegment(sketch, "E1.5.12.3", {"start": v(75, 180) * mm, "end": v(90, 180) * mm});
            skLineSegment(sketch, "E1.5.13.0", {"start": v(90, 195) * mm, "end": v(90, 210) * mm});
            skLineSegment(sketch, "E1.5.13.1", {"start": v(75, 195) * mm, "end": v(75, 210) * mm});
            skLineSegment(sketch, "E1.5.13.2", {"start": v(75, 210) * mm, "end": v(90, 210) * mm});
            skLineSegment(sketch, "E1.5.13.3", {"start": v(75, 195) * mm, "end": v(90, 195) * mm});
            skLineSegment(sketch, "E1.5.14.0", {"start": v(90, 210) * mm, "end": v(90, 225) * mm});
            skLineSegment(sketch, "E1.5.14.1", {"start": v(75, 210) * mm, "end": v(75, 225) * mm});
            skLineSegment(sketch, "E1.5.14.2", {"start": v(75, 225) * mm, "end": v(90, 225) * mm});
            skLineSegment(sketch, "E1.5.14.3", {"start": v(75, 210) * mm, "end": v(90, 210) * mm});
            skLineSegment(sketch, "E1.5.15.0", {"start": v(90, 225) * mm, "end": v(90, 240) * mm});
            skLineSegment(sketch, "E1.5.15.1", {"start": v(75, 225) * mm, "end": v(75, 240) * mm});
            skLineSegment(sketch, "E1.5.15.2", {"start": v(75, 240) * mm, "end": v(90, 240) * mm});
            skLineSegment(sketch, "E1.5.15.3", {"start": v(75, 225) * mm, "end": v(90, 225) * mm});
            skLineSegment(sketch, "E1.6.0.0", {"start": v(105, 0) * mm, "end": v(105, 15) * mm});
            skLineSegment(sketch, "E1.6.0.1", {"start": v(90, 0) * mm, "end": v(90, 15) * mm});
            skLineSegment(sketch, "E1.6.0.2", {"start": v(90, 15) * mm, "end": v(105, 15) * mm});
            skLineSegment(sketch, "E1.6.0.3", {"start": v(90, 0) * mm, "end": v(105, 0) * mm});
            skLineSegment(sketch, "E1.6.1.0", {"start": v(105, 15) * mm, "end": v(105, 30) * mm});
            skLineSegment(sketch, "E1.6.1.1", {"start": v(90, 15) * mm, "end": v(90, 30) * mm});
            skLineSegment(sketch, "E1.6.1.2", {"start": v(90, 30) * mm, "end": v(105, 30) * mm});
            skLineSegment(sketch, "E1.6.1.3", {"start": v(90, 15) * mm, "end": v(105, 15) * mm});
            skLineSegment(sketch, "E1.6.2.0", {"start": v(105, 30) * mm, "end": v(105, 45) * mm});
            skLineSegment(sketch, "E1.6.2.1", {"start": v(90, 30) * mm, "end": v(90, 45) * mm});
            skLineSegment(sketch, "E1.6.2.2", {"start": v(90, 45) * mm, "end": v(105, 45) * mm});
            skLineSegment(sketch, "E1.6.2.3", {"start": v(90, 30) * mm, "end": v(105, 30) * mm});
            skLineSegment(sketch, "E1.6.3.0", {"start": v(105, 45) * mm, "end": v(105, 60) * mm});
            skLineSegment(sketch, "E1.6.3.1", {"start": v(90, 45) * mm, "end": v(90, 60) * mm});
            skLineSegment(sketch, "E1.6.3.2", {"start": v(90, 60) * mm, "end": v(105, 60) * mm});
            skLineSegment(sketch, "E1.6.3.3", {"start": v(90, 45) * mm, "end": v(105, 45) * mm});
            skLineSegment(sketch, "E1.6.4.0", {"start": v(105, 60) * mm, "end": v(105, 75) * mm});
            skLineSegment(sketch, "E1.6.4.1", {"start": v(90, 60) * mm, "end": v(90, 75) * mm});
            skLineSegment(sketch, "E1.6.4.2", {"start": v(90, 75) * mm, "end": v(105, 75) * mm});
            skLineSegment(sketch, "E1.6.4.3", {"start": v(90, 60) * mm, "end": v(105, 60) * mm});
            skLineSegment(sketch, "E1.6.5.0", {"start": v(105, 75) * mm, "end": v(105, 90) * mm});
            skLineSegment(sketch, "E1.6.5.1", {"start": v(90, 75) * mm, "end": v(90, 90) * mm});
            skLineSegment(sketch, "E1.6.5.2", {"start": v(90, 90) * mm, "end": v(105, 90) * mm});
            skLineSegment(sketch, "E1.6.5.3", {"start": v(90, 75) * mm, "end": v(105, 75) * mm});
            skLineSegment(sketch, "E1.6.6.0", {"start": v(105, 90) * mm, "end": v(105, 105) * mm});
            skLineSegment(sketch, "E1.6.6.1", {"start": v(90, 90) * mm, "end": v(90, 105) * mm});
            skLineSegment(sketch, "E1.6.6.2", {"start": v(90, 105) * mm, "end": v(105, 105) * mm});
            skLineSegment(sketch, "E1.6.6.3", {"start": v(90, 90) * mm, "end": v(105, 90) * mm});
            skLineSegment(sketch, "E1.6.7.0", {"start": v(105, 105) * mm, "end": v(105, 120) * mm});
            skLineSegment(sketch, "E1.6.7.1", {"start": v(90, 105) * mm, "end": v(90, 120) * mm});
            skLineSegment(sketch, "E1.6.7.2", {"start": v(90, 120) * mm, "end": v(105, 120) * mm});
            skLineSegment(sketch, "E1.6.7.3", {"start": v(90, 105) * mm, "end": v(105, 105) * mm});
            skLineSegment(sketch, "E1.6.8.0", {"start": v(105, 120) * mm, "end": v(105, 135) * mm});
            skLineSegment(sketch, "E1.6.8.1", {"start": v(90, 120) * mm, "end": v(90, 135) * mm});
            skLineSegment(sketch, "E1.6.8.2", {"start": v(90, 135) * mm, "end": v(105, 135) * mm});
            skLineSegment(sketch, "E1.6.8.3", {"start": v(90, 120) * mm, "end": v(105, 120) * mm});
            skLineSegment(sketch, "E1.6.9.0", {"start": v(105, 135) * mm, "end": v(105, 150) * mm});
            skLineSegment(sketch, "E1.6.9.1", {"start": v(90, 135) * mm, "end": v(90, 150) * mm});
            skLineSegment(sketch, "E1.6.9.2", {"start": v(90, 150) * mm, "end": v(105, 150) * mm});
            skLineSegment(sketch, "E1.6.9.3", {"start": v(90, 135) * mm, "end": v(105, 135) * mm});
            skLineSegment(sketch, "E1.6.10.0", {"start": v(105, 150) * mm, "end": v(105, 165) * mm});
            skLineSegment(sketch, "E1.6.10.1", {"start": v(90, 150) * mm, "end": v(90, 165) * mm});
            skLineSegment(sketch, "E1.6.10.2", {"start": v(90, 165) * mm, "end": v(105, 165) * mm});
            skLineSegment(sketch, "E1.6.10.3", {"start": v(90, 150) * mm, "end": v(105, 150) * mm});
            skLineSegment(sketch, "E1.6.11.0", {"start": v(105, 165) * mm, "end": v(105, 180) * mm});
            skLineSegment(sketch, "E1.6.11.1", {"start": v(90, 165) * mm, "end": v(90, 180) * mm});
            skLineSegment(sketch, "E1.6.11.2", {"start": v(90, 180) * mm, "end": v(105, 180) * mm});
            skLineSegment(sketch, "E1.6.11.3", {"start": v(90, 165) * mm, "end": v(105, 165) * mm});
            skLineSegment(sketch, "E1.6.12.0", {"start": v(105, 180) * mm, "end": v(105, 195) * mm});
            skLineSegment(sketch, "E1.6.12.1", {"start": v(90, 180) * mm, "end": v(90, 195) * mm});
            skLineSegment(sketch, "E1.6.12.2", {"start": v(90, 195) * mm, "end": v(105, 195) * mm});
            skLineSegment(sketch, "E1.6.12.3", {"start": v(90, 180) * mm, "end": v(105, 180) * mm});
            skLineSegment(sketch, "E1.6.13.0", {"start": v(105, 195) * mm, "end": v(105, 210) * mm});
            skLineSegment(sketch, "E1.6.13.1", {"start": v(90, 195) * mm, "end": v(90, 210) * mm});
            skLineSegment(sketch, "E1.6.13.2", {"start": v(90, 210) * mm, "end": v(105, 210) * mm});
            skLineSegment(sketch, "E1.6.13.3", {"start": v(90, 195) * mm, "end": v(105, 195) * mm});
            skLineSegment(sketch, "E1.6.14.0", {"start": v(105, 210) * mm, "end": v(105, 225) * mm});
            skLineSegment(sketch, "E1.6.14.1", {"start": v(90, 210) * mm, "end": v(90, 225) * mm});
            skLineSegment(sketch, "E1.6.14.2", {"start": v(90, 225) * mm, "end": v(105, 225) * mm});
            skLineSegment(sketch, "E1.6.14.3", {"start": v(90, 210) * mm, "end": v(105, 210) * mm});
            skLineSegment(sketch, "E1.6.15.0", {"start": v(105, 225) * mm, "end": v(105, 240) * mm});
            skLineSegment(sketch, "E1.6.15.1", {"start": v(90, 225) * mm, "end": v(90, 240) * mm});
            skLineSegment(sketch, "E1.6.15.2", {"start": v(90, 240) * mm, "end": v(105, 240) * mm});
            skLineSegment(sketch, "E1.6.15.3", {"start": v(90, 225) * mm, "end": v(105, 225) * mm});
            skLineSegment(sketch, "E1.7.0.0", {"start": v(120, 0) * mm, "end": v(120, 15) * mm});
            skLineSegment(sketch, "E1.7.0.1", {"start": v(105, 0) * mm, "end": v(105, 15) * mm});
            skLineSegment(sketch, "E1.7.0.2", {"start": v(105, 15) * mm, "end": v(120, 15) * mm});
            skLineSegment(sketch, "E1.7.0.3", {"start": v(105, 0) * mm, "end": v(120, 0) * mm});
            skLineSegment(sketch, "E1.7.1.0", {"start": v(120, 15) * mm, "end": v(120, 30) * mm});
            skLineSegment(sketch, "E1.7.1.1", {"start": v(105, 15) * mm, "end": v(105, 30) * mm});
            skLineSegment(sketch, "E1.7.1.2", {"start": v(105, 30) * mm, "end": v(120, 30) * mm});
            skLineSegment(sketch, "E1.7.1.3", {"start": v(105, 15) * mm, "end": v(120, 15) * mm});
            skLineSegment(sketch, "E1.7.2.0", {"start": v(120, 30) * mm, "end": v(120, 45) * mm});
            skLineSegment(sketch, "E1.7.2.1", {"start": v(105, 30) * mm, "end": v(105, 45) * mm});
            skLineSegment(sketch, "E1.7.2.2", {"start": v(105, 45) * mm, "end": v(120, 45) * mm});
            skLineSegment(sketch, "E1.7.2.3", {"start": v(105, 30) * mm, "end": v(120, 30) * mm});
            skLineSegment(sketch, "E1.7.3.0", {"start": v(120, 45) * mm, "end": v(120, 60) * mm});
            skLineSegment(sketch, "E1.7.3.1", {"start": v(105, 45) * mm, "end": v(105, 60) * mm});
            skLineSegment(sketch, "E1.7.3.2", {"start": v(105, 60) * mm, "end": v(120, 60) * mm});
            skLineSegment(sketch, "E1.7.3.3", {"start": v(105, 45) * mm, "end": v(120, 45) * mm});
            skLineSegment(sketch, "E1.7.4.0", {"start": v(120, 60) * mm, "end": v(120, 75) * mm});
            skLineSegment(sketch, "E1.7.4.1", {"start": v(105, 60) * mm, "end": v(105, 75) * mm});
            skLineSegment(sketch, "E1.7.4.2", {"start": v(105, 75) * mm, "end": v(120, 75) * mm});
            skLineSegment(sketch, "E1.7.4.3", {"start": v(105, 60) * mm, "end": v(120, 60) * mm});
            skLineSegment(sketch, "E1.7.5.0", {"start": v(120, 75) * mm, "end": v(120, 90) * mm});
            skLineSegment(sketch, "E1.7.5.1", {"start": v(105, 75) * mm, "end": v(105, 90) * mm});
            skLineSegment(sketch, "E1.7.5.2", {"start": v(105, 90) * mm, "end": v(120, 90) * mm});
            skLineSegment(sketch, "E1.7.5.3", {"start": v(105, 75) * mm, "end": v(120, 75) * mm});
            skLineSegment(sketch, "E1.7.6.0", {"start": v(120, 90) * mm, "end": v(120, 105) * mm});
            skLineSegment(sketch, "E1.7.6.1", {"start": v(105, 90) * mm, "end": v(105, 105) * mm});
            skLineSegment(sketch, "E1.7.6.2", {"start": v(105, 105) * mm, "end": v(120, 105) * mm});
            skLineSegment(sketch, "E1.7.6.3", {"start": v(105, 90) * mm, "end": v(120, 90) * mm});
            skLineSegment(sketch, "E1.7.7.0", {"start": v(120, 105) * mm, "end": v(120, 120) * mm});
            skLineSegment(sketch, "E1.7.7.1", {"start": v(105, 105) * mm, "end": v(105, 120) * mm});
            skLineSegment(sketch, "E1.7.7.2", {"start": v(105, 120) * mm, "end": v(120, 120) * mm});
            skLineSegment(sketch, "E1.7.7.3", {"start": v(105, 105) * mm, "end": v(120, 105) * mm});
            skLineSegment(sketch, "E1.7.8.0", {"start": v(120, 120) * mm, "end": v(120, 135) * mm});
            skLineSegment(sketch, "E1.7.8.1", {"start": v(105, 120) * mm, "end": v(105, 135) * mm});
            skLineSegment(sketch, "E1.7.8.2", {"start": v(105, 135) * mm, "end": v(120, 135) * mm});
            skLineSegment(sketch, "E1.7.8.3", {"start": v(105, 120) * mm, "end": v(120, 120) * mm});
            skLineSegment(sketch, "E1.7.9.0", {"start": v(120, 135) * mm, "end": v(120, 150) * mm});
            skLineSegment(sketch, "E1.7.9.1", {"start": v(105, 135) * mm, "end": v(105, 150) * mm});
            skLineSegment(sketch, "E1.7.9.2", {"start": v(105, 150) * mm, "end": v(120, 150) * mm});
            skLineSegment(sketch, "E1.7.9.3", {"start": v(105, 135) * mm, "end": v(120, 135) * mm});
            skLineSegment(sketch, "E1.7.10.0", {"start": v(120, 150) * mm, "end": v(120, 165) * mm});
            skLineSegment(sketch, "E1.7.10.1", {"start": v(105, 150) * mm, "end": v(105, 165) * mm});
            skLineSegment(sketch, "E1.7.10.2", {"start": v(105, 165) * mm, "end": v(120, 165) * mm});
            skLineSegment(sketch, "E1.7.10.3", {"start": v(105, 150) * mm, "end": v(120, 150) * mm});
            skLineSegment(sketch, "E1.7.11.0", {"start": v(120, 165) * mm, "end": v(120, 180) * mm});
            skLineSegment(sketch, "E1.7.11.1", {"start": v(105, 165) * mm, "end": v(105, 180) * mm});
            skLineSegment(sketch, "E1.7.11.2", {"start": v(105, 180) * mm, "end": v(120, 180) * mm});
            skLineSegment(sketch, "E1.7.11.3", {"start": v(105, 165) * mm, "end": v(120, 165) * mm});
            skLineSegment(sketch, "E1.7.12.0", {"start": v(120, 180) * mm, "end": v(120, 195) * mm});
            skLineSegment(sketch, "E1.7.12.1", {"start": v(105, 180) * mm, "end": v(105, 195) * mm});
            skLineSegment(sketch, "E1.7.12.2", {"start": v(105, 195) * mm, "end": v(120, 195) * mm});
            skLineSegment(sketch, "E1.7.12.3", {"start": v(105, 180) * mm, "end": v(120, 180) * mm});
            skLineSegment(sketch, "E1.7.13.0", {"start": v(120, 195) * mm, "end": v(120, 210) * mm});
            skLineSegment(sketch, "E1.7.13.1", {"start": v(105, 195) * mm, "end": v(105, 210) * mm});
            skLineSegment(sketch, "E1.7.13.2", {"start": v(105, 210) * mm, "end": v(120, 210) * mm});
            skLineSegment(sketch, "E1.7.13.3", {"start": v(105, 195) * mm, "end": v(120, 195) * mm});
            skLineSegment(sketch, "E1.7.14.0", {"start": v(120, 210) * mm, "end": v(120, 225) * mm});
            skLineSegment(sketch, "E1.7.14.1", {"start": v(105, 210) * mm, "end": v(105, 225) * mm});
            skLineSegment(sketch, "E1.7.14.2", {"start": v(105, 225) * mm, "end": v(120, 225) * mm});
            skLineSegment(sketch, "E1.7.14.3", {"start": v(105, 210) * mm, "end": v(120, 210) * mm});
            skLineSegment(sketch, "E1.7.15.0", {"start": v(120, 225) * mm, "end": v(120, 240) * mm});
            skLineSegment(sketch, "E1.7.15.1", {"start": v(105, 225) * mm, "end": v(105, 240) * mm});
            skLineSegment(sketch, "E1.7.15.2", {"start": v(105, 240) * mm, "end": v(120, 240) * mm});
            skLineSegment(sketch, "E1.7.15.3", {"start": v(105, 225) * mm, "end": v(120, 225) * mm});
            skLineSegment(sketch, "E1.8.0.0", {"start": v(135, 0) * mm, "end": v(135, 15) * mm});
            skLineSegment(sketch, "E1.8.0.1", {"start": v(120, 0) * mm, "end": v(120, 15) * mm});
            skLineSegment(sketch, "E1.8.0.2", {"start": v(120, 15) * mm, "end": v(135, 15) * mm});
            skLineSegment(sketch, "E1.8.0.3", {"start": v(120, 0) * mm, "end": v(135, 0) * mm});
            skLineSegment(sketch, "E1.8.1.0", {"start": v(135, 15) * mm, "end": v(135, 30) * mm});
            skLineSegment(sketch, "E1.8.1.1", {"start": v(120, 15) * mm, "end": v(120, 30) * mm});
            skLineSegment(sketch, "E1.8.1.2", {"start": v(120, 30) * mm, "end": v(135, 30) * mm});
            skLineSegment(sketch, "E1.8.1.3", {"start": v(120, 15) * mm, "end": v(135, 15) * mm});
            skLineSegment(sketch, "E1.8.2.0", {"start": v(135, 30) * mm, "end": v(135, 45) * mm});
            skLineSegment(sketch, "E1.8.2.1", {"start": v(120, 30) * mm, "end": v(120, 45) * mm});
            skLineSegment(sketch, "E1.8.2.2", {"start": v(120, 45) * mm, "end": v(135, 45) * mm});
            skLineSegment(sketch, "E1.8.2.3", {"start": v(120, 30) * mm, "end": v(135, 30) * mm});
            skLineSegment(sketch, "E1.8.3.0", {"start": v(135, 45) * mm, "end": v(135, 60) * mm});
            skLineSegment(sketch, "E1.8.3.1", {"start": v(120, 45) * mm, "end": v(120, 60) * mm});
            skLineSegment(sketch, "E1.8.3.2", {"start": v(120, 60) * mm, "end": v(135, 60) * mm});
            skLineSegment(sketch, "E1.8.3.3", {"start": v(120, 45) * mm, "end": v(135, 45) * mm});
            skLineSegment(sketch, "E1.8.4.0", {"start": v(135, 60) * mm, "end": v(135, 75) * mm});
            skLineSegment(sketch, "E1.8.4.1", {"start": v(120, 60) * mm, "end": v(120, 75) * mm});
            skLineSegment(sketch, "E1.8.4.2", {"start": v(120, 75) * mm, "end": v(135, 75) * mm});
            skLineSegment(sketch, "E1.8.4.3", {"start": v(120, 60) * mm, "end": v(135, 60) * mm});
            skLineSegment(sketch, "E1.8.5.0", {"start": v(135, 75) * mm, "end": v(135, 90) * mm});
            skLineSegment(sketch, "E1.8.5.1", {"start": v(120, 75) * mm, "end": v(120, 90) * mm});
            skLineSegment(sketch, "E1.8.5.2", {"start": v(120, 90) * mm, "end": v(135, 90) * mm});
            skLineSegment(sketch, "E1.8.5.3", {"start": v(120, 75) * mm, "end": v(135, 75) * mm});
            skLineSegment(sketch, "E1.8.6.0", {"start": v(135, 90) * mm, "end": v(135, 105) * mm});
            skLineSegment(sketch, "E1.8.6.1", {"start": v(120, 90) * mm, "end": v(120, 105) * mm});
            skLineSegment(sketch, "E1.8.6.2", {"start": v(120, 105) * mm, "end": v(135, 105) * mm});
            skLineSegment(sketch, "E1.8.6.3", {"start": v(120, 90) * mm, "end": v(135, 90) * mm});
            skLineSegment(sketch, "E1.8.7.0", {"start": v(135, 105) * mm, "end": v(135, 120) * mm});
            skLineSegment(sketch, "E1.8.7.1", {"start": v(120, 105) * mm, "end": v(120, 120) * mm});
            skLineSegment(sketch, "E1.8.7.2", {"start": v(120, 120) * mm, "end": v(135, 120) * mm});
            skLineSegment(sketch, "E1.8.7.3", {"start": v(120, 105) * mm, "end": v(135, 105) * mm});
            skLineSegment(sketch, "E1.8.8.0", {"start": v(135, 120) * mm, "end": v(135, 135) * mm});
            skLineSegment(sketch, "E1.8.8.1", {"start": v(120, 120) * mm, "end": v(120, 135) * mm});
            skLineSegment(sketch, "E1.8.8.2", {"start": v(120, 135) * mm, "end": v(135, 135) * mm});
            skLineSegment(sketch, "E1.8.8.3", {"start": v(120, 120) * mm, "end": v(135, 120) * mm});
            skLineSegment(sketch, "E1.8.9.0", {"start": v(135, 135) * mm, "end": v(135, 150) * mm});
            skLineSegment(sketch, "E1.8.9.1", {"start": v(120, 135) * mm, "end": v(120, 150) * mm});
            skLineSegment(sketch, "E1.8.9.2", {"start": v(120, 150) * mm, "end": v(135, 150) * mm});
            skLineSegment(sketch, "E1.8.9.3", {"start": v(120, 135) * mm, "end": v(135, 135) * mm});
            skLineSegment(sketch, "E1.8.10.0", {"start": v(135, 150) * mm, "end": v(135, 165) * mm});
            skLineSegment(sketch, "E1.8.10.1", {"start": v(120, 150) * mm, "end": v(120, 165) * mm});
            skLineSegment(sketch, "E1.8.10.2", {"start": v(120, 165) * mm, "end": v(135, 165) * mm});
            skLineSegment(sketch, "E1.8.10.3", {"start": v(120, 150) * mm, "end": v(135, 150) * mm});
            skLineSegment(sketch, "E1.8.11.0", {"start": v(135, 165) * mm, "end": v(135, 180) * mm});
            skLineSegment(sketch, "E1.8.11.1", {"start": v(120, 165) * mm, "end": v(120, 180) * mm});
            skLineSegment(sketch, "E1.8.11.2", {"start": v(120, 180) * mm, "end": v(135, 180) * mm});
            skLineSegment(sketch, "E1.8.11.3", {"start": v(120, 165) * mm, "end": v(135, 165) * mm});
            skLineSegment(sketch, "E1.8.12.0", {"start": v(135, 180) * mm, "end": v(135, 195) * mm});
            skLineSegment(sketch, "E1.8.12.1", {"start": v(120, 180) * mm, "end": v(120, 195) * mm});
            skLineSegment(sketch, "E1.8.12.2", {"start": v(120, 195) * mm, "end": v(135, 195) * mm});
            skLineSegment(sketch, "E1.8.12.3", {"start": v(120, 180) * mm, "end": v(135, 180) * mm});
            skLineSegment(sketch, "E1.8.13.0", {"start": v(135, 195) * mm, "end": v(135, 210) * mm});
            skLineSegment(sketch, "E1.8.13.1", {"start": v(120, 195) * mm, "end": v(120, 210) * mm});
            skLineSegment(sketch, "E1.8.13.2", {"start": v(120, 210) * mm, "end": v(135, 210) * mm});
            skLineSegment(sketch, "E1.8.13.3", {"start": v(120, 195) * mm, "end": v(135, 195) * mm});
            skLineSegment(sketch, "E1.8.14.0", {"start": v(135, 210) * mm, "end": v(135, 225) * mm});
            skLineSegment(sketch, "E1.8.14.1", {"start": v(120, 210) * mm, "end": v(120, 225) * mm});
            skLineSegment(sketch, "E1.8.14.2", {"start": v(120, 225) * mm, "end": v(135, 225) * mm});
            skLineSegment(sketch, "E1.8.14.3", {"start": v(120, 210) * mm, "end": v(135, 210) * mm});
            skLineSegment(sketch, "E1.8.15.0", {"start": v(135, 225) * mm, "end": v(135, 240) * mm});
            skLineSegment(sketch, "E1.8.15.1", {"start": v(120, 225) * mm, "end": v(120, 240) * mm});
            skLineSegment(sketch, "E1.8.15.2", {"start": v(120, 240) * mm, "end": v(135, 240) * mm});
            skLineSegment(sketch, "E1.8.15.3", {"start": v(120, 225) * mm, "end": v(135, 225) * mm});
            skLineSegment(sketch, "E1.9.0.0", {"start": v(150, 0) * mm, "end": v(150, 15) * mm});
            skLineSegment(sketch, "E1.9.0.1", {"start": v(135, 0) * mm, "end": v(135, 15) * mm});
            skLineSegment(sketch, "E1.9.0.2", {"start": v(135, 15) * mm, "end": v(150, 15) * mm});
            skLineSegment(sketch, "E1.9.0.3", {"start": v(135, 0) * mm, "end": v(150, 0) * mm});
            skLineSegment(sketch, "E1.9.1.0", {"start": v(150, 15) * mm, "end": v(150, 30) * mm});
            skLineSegment(sketch, "E1.9.1.1", {"start": v(135, 15) * mm, "end": v(135, 30) * mm});
            skLineSegment(sketch, "E1.9.1.2", {"start": v(135, 30) * mm, "end": v(150, 30) * mm});
            skLineSegment(sketch, "E1.9.1.3", {"start": v(135, 15) * mm, "end": v(150, 15) * mm});
            skLineSegment(sketch, "E1.9.2.0", {"start": v(150, 30) * mm, "end": v(150, 45) * mm});
            skLineSegment(sketch, "E1.9.2.1", {"start": v(135, 30) * mm, "end": v(135, 45) * mm});
            skLineSegment(sketch, "E1.9.2.2", {"start": v(135, 45) * mm, "end": v(150, 45) * mm});
            skLineSegment(sketch, "E1.9.2.3", {"start": v(135, 30) * mm, "end": v(150, 30) * mm});
            skLineSegment(sketch, "E1.9.3.0", {"start": v(150, 45) * mm, "end": v(150, 60) * mm});
            skLineSegment(sketch, "E1.9.3.1", {"start": v(135, 45) * mm, "end": v(135, 60) * mm});
            skLineSegment(sketch, "E1.9.3.2", {"start": v(135, 60) * mm, "end": v(150, 60) * mm});
            skLineSegment(sketch, "E1.9.3.3", {"start": v(135, 45) * mm, "end": v(150, 45) * mm});
            skLineSegment(sketch, "E1.9.4.0", {"start": v(150, 60) * mm, "end": v(150, 75) * mm});
            skLineSegment(sketch, "E1.9.4.1", {"start": v(135, 60) * mm, "end": v(135, 75) * mm});
            skLineSegment(sketch, "E1.9.4.2", {"start": v(135, 75) * mm, "end": v(150, 75) * mm});
            skLineSegment(sketch, "E1.9.4.3", {"start": v(135, 60) * mm, "end": v(150, 60) * mm});
            skLineSegment(sketch, "E1.9.5.0", {"start": v(150, 75) * mm, "end": v(150, 90) * mm});
            skLineSegment(sketch, "E1.9.5.1", {"start": v(135, 75) * mm, "end": v(135, 90) * mm});
            skLineSegment(sketch, "E1.9.5.2", {"start": v(135, 90) * mm, "end": v(150, 90) * mm});
            skLineSegment(sketch, "E1.9.5.3", {"start": v(135, 75) * mm, "end": v(150, 75) * mm});
            skLineSegment(sketch, "E1.9.6.0", {"start": v(150, 90) * mm, "end": v(150, 105) * mm});
            skLineSegment(sketch, "E1.9.6.1", {"start": v(135, 90) * mm, "end": v(135, 105) * mm});
            skLineSegment(sketch, "E1.9.6.2", {"start": v(135, 105) * mm, "end": v(150, 105) * mm});
            skLineSegment(sketch, "E1.9.6.3", {"start": v(135, 90) * mm, "end": v(150, 90) * mm});
            skLineSegment(sketch, "E1.9.7.0", {"start": v(150, 105) * mm, "end": v(150, 120) * mm});
            skLineSegment(sketch, "E1.9.7.1", {"start": v(135, 105) * mm, "end": v(135, 120) * mm});
            skLineSegment(sketch, "E1.9.7.2", {"start": v(135, 120) * mm, "end": v(150, 120) * mm});
            skLineSegment(sketch, "E1.9.7.3", {"start": v(135, 105) * mm, "end": v(150, 105) * mm});
            skLineSegment(sketch, "E1.9.8.0", {"start": v(150, 120) * mm, "end": v(150, 135) * mm});
            skLineSegment(sketch, "E1.9.8.1", {"start": v(135, 120) * mm, "end": v(135, 135) * mm});
            skLineSegment(sketch, "E1.9.8.2", {"start": v(135, 135) * mm, "end": v(150, 135) * mm});
            skLineSegment(sketch, "E1.9.8.3", {"start": v(135, 120) * mm, "end": v(150, 120) * mm});
            skLineSegment(sketch, "E1.9.9.0", {"start": v(150, 135) * mm, "end": v(150, 150) * mm});
            skLineSegment(sketch, "E1.9.9.1", {"start": v(135, 135) * mm, "end": v(135, 150) * mm});
            skLineSegment(sketch, "E1.9.9.2", {"start": v(135, 150) * mm, "end": v(150, 150) * mm});
            skLineSegment(sketch, "E1.9.9.3", {"start": v(135, 135) * mm, "end": v(150, 135) * mm});
            skLineSegment(sketch, "E1.9.10.0", {"start": v(150, 150) * mm, "end": v(150, 165) * mm});
            skLineSegment(sketch, "E1.9.10.1", {"start": v(135, 150) * mm, "end": v(135, 165) * mm});
            skLineSegment(sketch, "E1.9.10.2", {"start": v(135, 165) * mm, "end": v(150, 165) * mm});
            skLineSegment(sketch, "E1.9.10.3", {"start": v(135, 150) * mm, "end": v(150, 150) * mm});
            skLineSegment(sketch, "E1.9.11.0", {"start": v(150, 165) * mm, "end": v(150, 180) * mm});
            skLineSegment(sketch, "E1.9.11.1", {"start": v(135, 165) * mm, "end": v(135, 180) * mm});
            skLineSegment(sketch, "E1.9.11.2", {"start": v(135, 180) * mm, "end": v(150, 180) * mm});
            skLineSegment(sketch, "E1.9.11.3", {"start": v(135, 165) * mm, "end": v(150, 165) * mm});
            skLineSegment(sketch, "E1.9.12.0", {"start": v(150, 180) * mm, "end": v(150, 195) * mm});
            skLineSegment(sketch, "E1.9.12.1", {"start": v(135, 180) * mm, "end": v(135, 195) * mm});
            skLineSegment(sketch, "E1.9.12.2", {"start": v(135, 195) * mm, "end": v(150, 195) * mm});
            skLineSegment(sketch, "E1.9.12.3", {"start": v(135, 180) * mm, "end": v(150, 180) * mm});
            skLineSegment(sketch, "E1.9.13.0", {"start": v(150, 195) * mm, "end": v(150, 210) * mm});
            skLineSegment(sketch, "E1.9.13.1", {"start": v(135, 195) * mm, "end": v(135, 210) * mm});
            skLineSegment(sketch, "E1.9.13.2", {"start": v(135, 210) * mm, "end": v(150, 210) * mm});
            skLineSegment(sketch, "E1.9.13.3", {"start": v(135, 195) * mm, "end": v(150, 195) * mm});
            skLineSegment(sketch, "E1.9.14.0", {"start": v(150, 210) * mm, "end": v(150, 225) * mm});
            skLineSegment(sketch, "E1.9.14.1", {"start": v(135, 210) * mm, "end": v(135, 225) * mm});
            skLineSegment(sketch, "E1.9.14.2", {"start": v(135, 225) * mm, "end": v(150, 225) * mm});
            skLineSegment(sketch, "E1.9.14.3", {"start": v(135, 210) * mm, "end": v(150, 210) * mm});
            skLineSegment(sketch, "E1.9.15.0", {"start": v(150, 225) * mm, "end": v(150, 240) * mm});
            skLineSegment(sketch, "E1.9.15.1", {"start": v(135, 225) * mm, "end": v(135, 240) * mm});
            skLineSegment(sketch, "E1.9.15.2", {"start": v(135, 240) * mm, "end": v(150, 240) * mm});
            skLineSegment(sketch, "E1.9.15.3", {"start": v(135, 225) * mm, "end": v(150, 225) * mm});
            skLineSegment(sketch, "E1.10.0.0", {"start": v(165, 0) * mm, "end": v(165, 15) * mm});
            skLineSegment(sketch, "E1.10.0.1", {"start": v(150, 0) * mm, "end": v(150, 15) * mm});
            skLineSegment(sketch, "E1.10.0.2", {"start": v(150, 15) * mm, "end": v(165, 15) * mm});
            skLineSegment(sketch, "E1.10.0.3", {"start": v(150, 0) * mm, "end": v(165, 0) * mm});
            skLineSegment(sketch, "E1.10.1.0", {"start": v(165, 15) * mm, "end": v(165, 30) * mm});
            skLineSegment(sketch, "E1.10.1.1", {"start": v(150, 15) * mm, "end": v(150, 30) * mm});
            skLineSegment(sketch, "E1.10.1.2", {"start": v(150, 30) * mm, "end": v(165, 30) * mm});
            skLineSegment(sketch, "E1.10.1.3", {"start": v(150, 15) * mm, "end": v(165, 15) * mm});
            skLineSegment(sketch, "E1.10.2.0", {"start": v(165, 30) * mm, "end": v(165, 45) * mm});
            skLineSegment(sketch, "E1.10.2.1", {"start": v(150, 30) * mm, "end": v(150, 45) * mm});
            skLineSegment(sketch, "E1.10.2.2", {"start": v(150, 45) * mm, "end": v(165, 45) * mm});
            skLineSegment(sketch, "E1.10.2.3", {"start": v(150, 30) * mm, "end": v(165, 30) * mm});
            skLineSegment(sketch, "E1.10.3.0", {"start": v(165, 45) * mm, "end": v(165, 60) * mm});
            skLineSegment(sketch, "E1.10.3.1", {"start": v(150, 45) * mm, "end": v(150, 60) * mm});
            skLineSegment(sketch, "E1.10.3.2", {"start": v(150, 60) * mm, "end": v(165, 60) * mm});
            skLineSegment(sketch, "E1.10.3.3", {"start": v(150, 45) * mm, "end": v(165, 45) * mm});
            skLineSegment(sketch, "E1.10.4.0", {"start": v(165, 60) * mm, "end": v(165, 75) * mm});
            skLineSegment(sketch, "E1.10.4.1", {"start": v(150, 60) * mm, "end": v(150, 75) * mm});
            skLineSegment(sketch, "E1.10.4.2", {"start": v(150, 75) * mm, "end": v(165, 75) * mm});
            skLineSegment(sketch, "E1.10.4.3", {"start": v(150, 60) * mm, "end": v(165, 60) * mm});
            skLineSegment(sketch, "E1.10.5.0", {"start": v(165, 75) * mm, "end": v(165, 90) * mm});
            skLineSegment(sketch, "E1.10.5.1", {"start": v(150, 75) * mm, "end": v(150, 90) * mm});
            skLineSegment(sketch, "E1.10.5.2", {"start": v(150, 90) * mm, "end": v(165, 90) * mm});
            skLineSegment(sketch, "E1.10.5.3", {"start": v(150, 75) * mm, "end": v(165, 75) * mm});
            skLineSegment(sketch, "E1.10.6.0", {"start": v(165, 90) * mm, "end": v(165, 105) * mm});
            skLineSegment(sketch, "E1.10.6.1", {"start": v(150, 90) * mm, "end": v(150, 105) * mm});
            skLineSegment(sketch, "E1.10.6.2", {"start": v(150, 105) * mm, "end": v(165, 105) * mm});
            skLineSegment(sketch, "E1.10.6.3", {"start": v(150, 90) * mm, "end": v(165, 90) * mm});
            skLineSegment(sketch, "E1.10.7.0", {"start": v(165, 105) * mm, "end": v(165, 120) * mm});
            skLineSegment(sketch, "E1.10.7.1", {"start": v(150, 105) * mm, "end": v(150, 120) * mm});
            skLineSegment(sketch, "E1.10.7.2", {"start": v(150, 120) * mm, "end": v(165, 120) * mm});
            skLineSegment(sketch, "E1.10.7.3", {"start": v(150, 105) * mm, "end": v(165, 105) * mm});
            skLineSegment(sketch, "E1.10.8.0", {"start": v(165, 120) * mm, "end": v(165, 135) * mm});
            skLineSegment(sketch, "E1.10.8.1", {"start": v(150, 120) * mm, "end": v(150, 135) * mm});
            skLineSegment(sketch, "E1.10.8.2", {"start": v(150, 135) * mm, "end": v(165, 135) * mm});
            skLineSegment(sketch, "E1.10.8.3", {"start": v(150, 120) * mm, "end": v(165, 120) * mm});
            skLineSegment(sketch, "E1.10.9.0", {"start": v(165, 135) * mm, "end": v(165, 150) * mm});
            skLineSegment(sketch, "E1.10.9.1", {"start": v(150, 135) * mm, "end": v(150, 150) * mm});
            skLineSegment(sketch, "E1.10.9.2", {"start": v(150, 150) * mm, "end": v(165, 150) * mm});
            skLineSegment(sketch, "E1.10.9.3", {"start": v(150, 135) * mm, "end": v(165, 135) * mm});
            skLineSegment(sketch, "E1.10.10.0", {"start": v(165, 150) * mm, "end": v(165, 165) * mm});
            skLineSegment(sketch, "E1.10.10.1", {"start": v(150, 150) * mm, "end": v(150, 165) * mm});
            skLineSegment(sketch, "E1.10.10.2", {"start": v(150, 165) * mm, "end": v(165, 165) * mm});
            skLineSegment(sketch, "E1.10.10.3", {"start": v(150, 150) * mm, "end": v(165, 150) * mm});
            skLineSegment(sketch, "E1.10.11.0", {"start": v(165, 165) * mm, "end": v(165, 180) * mm});
            skLineSegment(sketch, "E1.10.11.1", {"start": v(150, 165) * mm, "end": v(150, 180) * mm});
            skLineSegment(sketch, "E1.10.11.2", {"start": v(150, 180) * mm, "end": v(165, 180) * mm});
            skLineSegment(sketch, "E1.10.11.3", {"start": v(150, 165) * mm, "end": v(165, 165) * mm});
            skLineSegment(sketch, "E1.10.12.0", {"start": v(165, 180) * mm, "end": v(165, 195) * mm});
            skLineSegment(sketch, "E1.10.12.1", {"start": v(150, 180) * mm, "end": v(150, 195) * mm});
            skLineSegment(sketch, "E1.10.12.2", {"start": v(150, 195) * mm, "end": v(165, 195) * mm});
            skLineSegment(sketch, "E1.10.12.3", {"start": v(150, 180) * mm, "end": v(165, 180) * mm});
            skLineSegment(sketch, "E1.10.13.0", {"start": v(165, 195) * mm, "end": v(165, 210) * mm});
            skLineSegment(sketch, "E1.10.13.1", {"start": v(150, 195) * mm, "end": v(150, 210) * mm});
            skLineSegment(sketch, "E1.10.13.2", {"start": v(150, 210) * mm, "end": v(165, 210) * mm});
            skLineSegment(sketch, "E1.10.13.3", {"start": v(150, 195) * mm, "end": v(165, 195) * mm});
            skLineSegment(sketch, "E1.10.14.0", {"start": v(165, 210) * mm, "end": v(165, 225) * mm});
            skLineSegment(sketch, "E1.10.14.1", {"start": v(150, 210) * mm, "end": v(150, 225) * mm});
            skLineSegment(sketch, "E1.10.14.2", {"start": v(150, 225) * mm, "end": v(165, 225) * mm});
            skLineSegment(sketch, "E1.10.14.3", {"start": v(150, 210) * mm, "end": v(165, 210) * mm});
            skLineSegment(sketch, "E1.10.15.0", {"start": v(165, 225) * mm, "end": v(165, 240) * mm});
            skLineSegment(sketch, "E1.10.15.1", {"start": v(150, 225) * mm, "end": v(150, 240) * mm});
            skLineSegment(sketch, "E1.10.15.2", {"start": v(150, 240) * mm, "end": v(165, 240) * mm});
            skLineSegment(sketch, "E1.10.15.3", {"start": v(150, 225) * mm, "end": v(165, 225) * mm});
            skLineSegment(sketch, "E1.11.0.0", {"start": v(180, 0) * mm, "end": v(180, 15) * mm});
            skLineSegment(sketch, "E1.11.0.1", {"start": v(165, 0) * mm, "end": v(165, 15) * mm});
            skLineSegment(sketch, "E1.11.0.2", {"start": v(165, 15) * mm, "end": v(180, 15) * mm});
            skLineSegment(sketch, "E1.11.0.3", {"start": v(165, 0) * mm, "end": v(180, 0) * mm});
            skLineSegment(sketch, "E1.11.1.0", {"start": v(180, 15) * mm, "end": v(180, 30) * mm});
            skLineSegment(sketch, "E1.11.1.1", {"start": v(165, 15) * mm, "end": v(165, 30) * mm});
            skLineSegment(sketch, "E1.11.1.2", {"start": v(165, 30) * mm, "end": v(180, 30) * mm});
            skLineSegment(sketch, "E1.11.1.3", {"start": v(165, 15) * mm, "end": v(180, 15) * mm});
            skLineSegment(sketch, "E1.11.2.0", {"start": v(180, 30) * mm, "end": v(180, 45) * mm});
            skLineSegment(sketch, "E1.11.2.1", {"start": v(165, 30) * mm, "end": v(165, 45) * mm});
            skLineSegment(sketch, "E1.11.2.2", {"start": v(165, 45) * mm, "end": v(180, 45) * mm});
            skLineSegment(sketch, "E1.11.2.3", {"start": v(165, 30) * mm, "end": v(180, 30) * mm});
            skLineSegment(sketch, "E1.11.3.0", {"start": v(180, 45) * mm, "end": v(180, 60) * mm});
            skLineSegment(sketch, "E1.11.3.1", {"start": v(165, 45) * mm, "end": v(165, 60) * mm});
            skLineSegment(sketch, "E1.11.3.2", {"start": v(165, 60) * mm, "end": v(180, 60) * mm});
            skLineSegment(sketch, "E1.11.3.3", {"start": v(165, 45) * mm, "end": v(180, 45) * mm});
            skLineSegment(sketch, "E1.11.4.0", {"start": v(180, 60) * mm, "end": v(180, 75) * mm});
            skLineSegment(sketch, "E1.11.4.1", {"start": v(165, 60) * mm, "end": v(165, 75) * mm});
            skLineSegment(sketch, "E1.11.4.2", {"start": v(165, 75) * mm, "end": v(180, 75) * mm});
            skLineSegment(sketch, "E1.11.4.3", {"start": v(165, 60) * mm, "end": v(180, 60) * mm});
            skLineSegment(sketch, "E1.11.5.0", {"start": v(180, 75) * mm, "end": v(180, 90) * mm});
            skLineSegment(sketch, "E1.11.5.1", {"start": v(165, 75) * mm, "end": v(165, 90) * mm});
            skLineSegment(sketch, "E1.11.5.2", {"start": v(165, 90) * mm, "end": v(180, 90) * mm});
            skLineSegment(sketch, "E1.11.5.3", {"start": v(165, 75) * mm, "end": v(180, 75) * mm});
            skLineSegment(sketch, "E1.11.6.0", {"start": v(180, 90) * mm, "end": v(180, 105) * mm});
            skLineSegment(sketch, "E1.11.6.1", {"start": v(165, 90) * mm, "end": v(165, 105) * mm});
            skLineSegment(sketch, "E1.11.6.2", {"start": v(165, 105) * mm, "end": v(180, 105) * mm});
            skLineSegment(sketch, "E1.11.6.3", {"start": v(165, 90) * mm, "end": v(180, 90) * mm});
            skLineSegment(sketch, "E1.11.7.0", {"start": v(180, 105) * mm, "end": v(180, 120) * mm});
            skLineSegment(sketch, "E1.11.7.1", {"start": v(165, 105) * mm, "end": v(165, 120) * mm});
            skLineSegment(sketch, "E1.11.7.2", {"start": v(165, 120) * mm, "end": v(180, 120) * mm});
            skLineSegment(sketch, "E1.11.7.3", {"start": v(165, 105) * mm, "end": v(180, 105) * mm});
            skLineSegment(sketch, "E1.11.8.0", {"start": v(180, 120) * mm, "end": v(180, 135) * mm});
            skLineSegment(sketch, "E1.11.8.1", {"start": v(165, 120) * mm, "end": v(165, 135) * mm});
            skLineSegment(sketch, "E1.11.8.2", {"start": v(165, 135) * mm, "end": v(180, 135) * mm});
            skLineSegment(sketch, "E1.11.8.3", {"start": v(165, 120) * mm, "end": v(180, 120) * mm});
            skLineSegment(sketch, "E1.11.9.0", {"start": v(180, 135) * mm, "end": v(180, 150) * mm});
            skLineSegment(sketch, "E1.11.9.1", {"start": v(165, 135) * mm, "end": v(165, 150) * mm});
            skLineSegment(sketch, "E1.11.9.2", {"start": v(165, 150) * mm, "end": v(180, 150) * mm});
            skLineSegment(sketch, "E1.11.9.3", {"start": v(165, 135) * mm, "end": v(180, 135) * mm});
            skLineSegment(sketch, "E1.11.10.0", {"start": v(180, 150) * mm, "end": v(180, 165) * mm});
            skLineSegment(sketch, "E1.11.10.1", {"start": v(165, 150) * mm, "end": v(165, 165) * mm});
            skLineSegment(sketch, "E1.11.10.2", {"start": v(165, 165) * mm, "end": v(180, 165) * mm});
            skLineSegment(sketch, "E1.11.10.3", {"start": v(165, 150) * mm, "end": v(180, 150) * mm});
            skLineSegment(sketch, "E1.11.11.0", {"start": v(180, 165) * mm, "end": v(180, 180) * mm});
            skLineSegment(sketch, "E1.11.11.1", {"start": v(165, 165) * mm, "end": v(165, 180) * mm});
            skLineSegment(sketch, "E1.11.11.2", {"start": v(165, 180) * mm, "end": v(180, 180) * mm});
            skLineSegment(sketch, "E1.11.11.3", {"start": v(165, 165) * mm, "end": v(180, 165) * mm});
            skLineSegment(sketch, "E1.11.12.0", {"start": v(180, 180) * mm, "end": v(180, 195) * mm});
            skLineSegment(sketch, "E1.11.12.1", {"start": v(165, 180) * mm, "end": v(165, 195) * mm});
            skLineSegment(sketch, "E1.11.12.2", {"start": v(165, 195) * mm, "end": v(180, 195) * mm});
            skLineSegment(sketch, "E1.11.12.3", {"start": v(165, 180) * mm, "end": v(180, 180) * mm});
            skLineSegment(sketch, "E1.11.13.0", {"start": v(180, 195) * mm, "end": v(180, 210) * mm});
            skLineSegment(sketch, "E1.11.13.1", {"start": v(165, 195) * mm, "end": v(165, 210) * mm});
            skLineSegment(sketch, "E1.11.13.2", {"start": v(165, 210) * mm, "end": v(180, 210) * mm});
            skLineSegment(sketch, "E1.11.13.3", {"start": v(165, 195) * mm, "end": v(180, 195) * mm});
            skLineSegment(sketch, "E1.11.14.0", {"start": v(180, 210) * mm, "end": v(180, 225) * mm});
            skLineSegment(sketch, "E1.11.14.1", {"start": v(165, 210) * mm, "end": v(165, 225) * mm});
            skLineSegment(sketch, "E1.11.14.2", {"start": v(165, 225) * mm, "end": v(180, 225) * mm});
            skLineSegment(sketch, "E1.11.14.3", {"start": v(165, 210) * mm, "end": v(180, 210) * mm});
            skLineSegment(sketch, "E1.11.15.0", {"start": v(180, 225) * mm, "end": v(180, 240) * mm});
            skLineSegment(sketch, "E1.11.15.1", {"start": v(165, 225) * mm, "end": v(165, 240) * mm});
            skLineSegment(sketch, "E1.11.15.2", {"start": v(165, 240) * mm, "end": v(180, 240) * mm});
            skLineSegment(sketch, "E1.11.15.3", {"start": v(165, 225) * mm, "end": v(180, 225) * mm});
            skLineSegment(sketch, "E1.direction1", {"start": v(0, 0) * mm, "end": v(15, 0) * mm, "construction": true});
            skLineSegment(sketch, "E1.direction2", {"start": v(0, 0) * mm, "end": v(0, 15) * mm, "construction": true});
            skSolve(sketch);
        }
        {
            var Q0;
            Q0=makeQuery(id+"F0.imprint","IMPRINT",FACE,{"disambiguationData":[TD([[makeQuery(id+"F0.imprint","IMPRINT",EDGE,{"derivedFrom":sQuery(id+"F0.wireOp",EDGE,"E0.bottom")}),1.0]])]});
            var Q1;
            Q1=makeQuery(id+"F0.imprint","IMPRINT",FACE,{"disambiguationData":[TD([[makeQuery(id+"F0.imprint","IMPRINT",EDGE,{"derivedFrom":sQuery(id+"F0.wireOp",EDGE,"E1.2.0.1")}),-1.0]])]});
            var Q2;
            Q2=makeQuery(id+"F0.imprint","IMPRINT",FACE,{"disambiguationData":[TD([[makeQuery(id+"F0.imprint","IMPRINT",EDGE,{"derivedFrom":sQuery(id+"F0.wireOp",EDGE,"E1.4.0.1")}),-1.0]])]});
            var Q3;
            Q3=makeQuery(id+"F0.imprint","IMPRINT",FACE,{"disambiguationData":[TD([[makeQuery(id+"F0.imprint","IMPRINT",EDGE,{"derivedFrom":sQuery(id+"F0.wireOp",EDGE,"E1.6.0.1")}),-1.0]])]});
            extrude(context, id + "F1", {"entities" : qUnion([Q0, Q1, Q2, Q3]), "depth" : 15 * mm, "offsetDistance" : 25 * mm});
        }
    });
